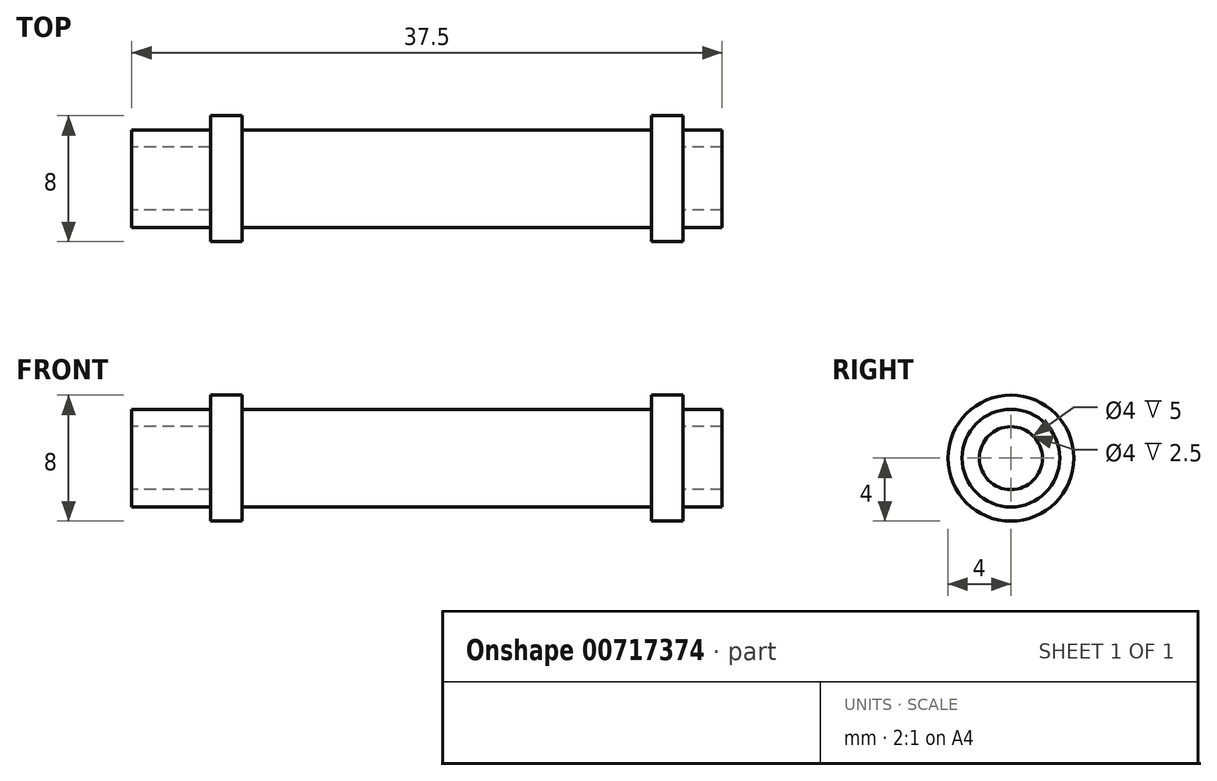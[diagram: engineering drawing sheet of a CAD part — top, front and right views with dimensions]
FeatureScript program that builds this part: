
annotation { "Feature Type Name" : "Feature", "Feature Type Description" : "" }
export const myFeature = defineFeature(function(context is Context, id is Id, definition is map)
    precondition{}
    {
        {
            var Q0;
            Q0=qCreatedBy(makeId("Front.planeOp"),FACE);
            var sketch = newSketch(context, id + "F0", { "sketchPlane" : qUnion([Q0])});
            skLineSegment(sketch, "E0", {"start": v(-14.88, 0) * mm, "end": v(32.5, 0) * mm, "construction": true});
            skLineSegment(sketch, "E1", {"start": v(-2.5, 3.1) * mm, "end": v(2.5, 3.1) * mm});
            skLineSegment(sketch, "E2", {"start": v(2.5, 3.1) * mm, "end": v(2.5, 4) * mm});
            skLineSegment(sketch, "E3", {"start": v(2.5, 4) * mm, "end": v(4.5, 4) * mm});
            skLineSegment(sketch, "E4", {"start": v(4.5, 4) * mm, "end": v(4.5, 3.1) * mm});
            skLineSegment(sketch, "E5", {"start": v(4.5, 3.1) * mm, "end": v(30.5, 3.1) * mm});
            skLineSegment(sketch, "E6", {"start": v(-2.5, 3.1) * mm, "end": v(-2.5, 2) * mm});
            skLineSegment(sketch, "E7", {"start": v(-2.5, 2) * mm, "end": v(2.5, 2) * mm});
            skLineSegment(sketch, "E8", {"start": v(2.5, 2) * mm, "end": v(2.5, 0) * mm});
            skLineSegment(sketch, "E9", {"start": v(2.5, 0) * mm, "end": v(95, 0) * mm});
            skLineSegment(sketch, "E10", {"start": v(50, 21.64) * mm, "end": v(50, -26.7) * mm, "construction": true});
            skLineSegment(sketch, "E11", {"start": v(32.5, 3.1) * mm, "end": v(32.5, 4) * mm});
            skLineSegment(sketch, "E12", {"start": v(32.5, 4) * mm, "end": v(30.5, 4) * mm});
            skLineSegment(sketch, "E13", {"start": v(30.5, 4) * mm, "end": v(30.5, 3.1) * mm});
            skLineSegment(sketch, "E14.trimOffspring", {"start": v(32.5, 3.1) * mm, "end": v(35, 3.1) * mm});
            skLineSegment(sketch, "E15", {"start": v(35, 3.1) * mm, "end": v(35, 2) * mm});
            skLineSegment(sketch, "E16", {"start": v(35, 2) * mm, "end": v(32.5, 2) * mm});
            skLineSegment(sketch, "E17", {"start": v(32.5, 2) * mm, "end": v(32.5, 0) * mm});
            skLineSegment(sketch, "E18.trimOffspring", {"start": v(50, 0) * mm, "end": v(95, 0) * mm, "construction": true});
            skPoint(sketch, "E19.orphan", {"position": v(102.43, 0) * mm});
            skSolve(sketch);
        }
        {
            var Q0;
            Q0=makeQuery(id+"F0.imprint","IMPRINT",FACE,{"disambiguationData":[TD([[makeQuery(id+"F0.imprint","IMPRINT",EDGE,{"derivedFrom":sQuery(id+"F0.wireOp",EDGE,"E1")}),-1.0]])]});
            var Q1;
            Q1=sQuery(id+"F0.wireOp",EDGE,"E0");
            revolve(context, id + "F1", {"surfaceOperationType" : NewSurfaceOperationType.NEW, "entities" : qUnion([Q0]), "axis" : qUnion([Q1]), "revolveType" : RevolveType.FULL});
        }
    });
